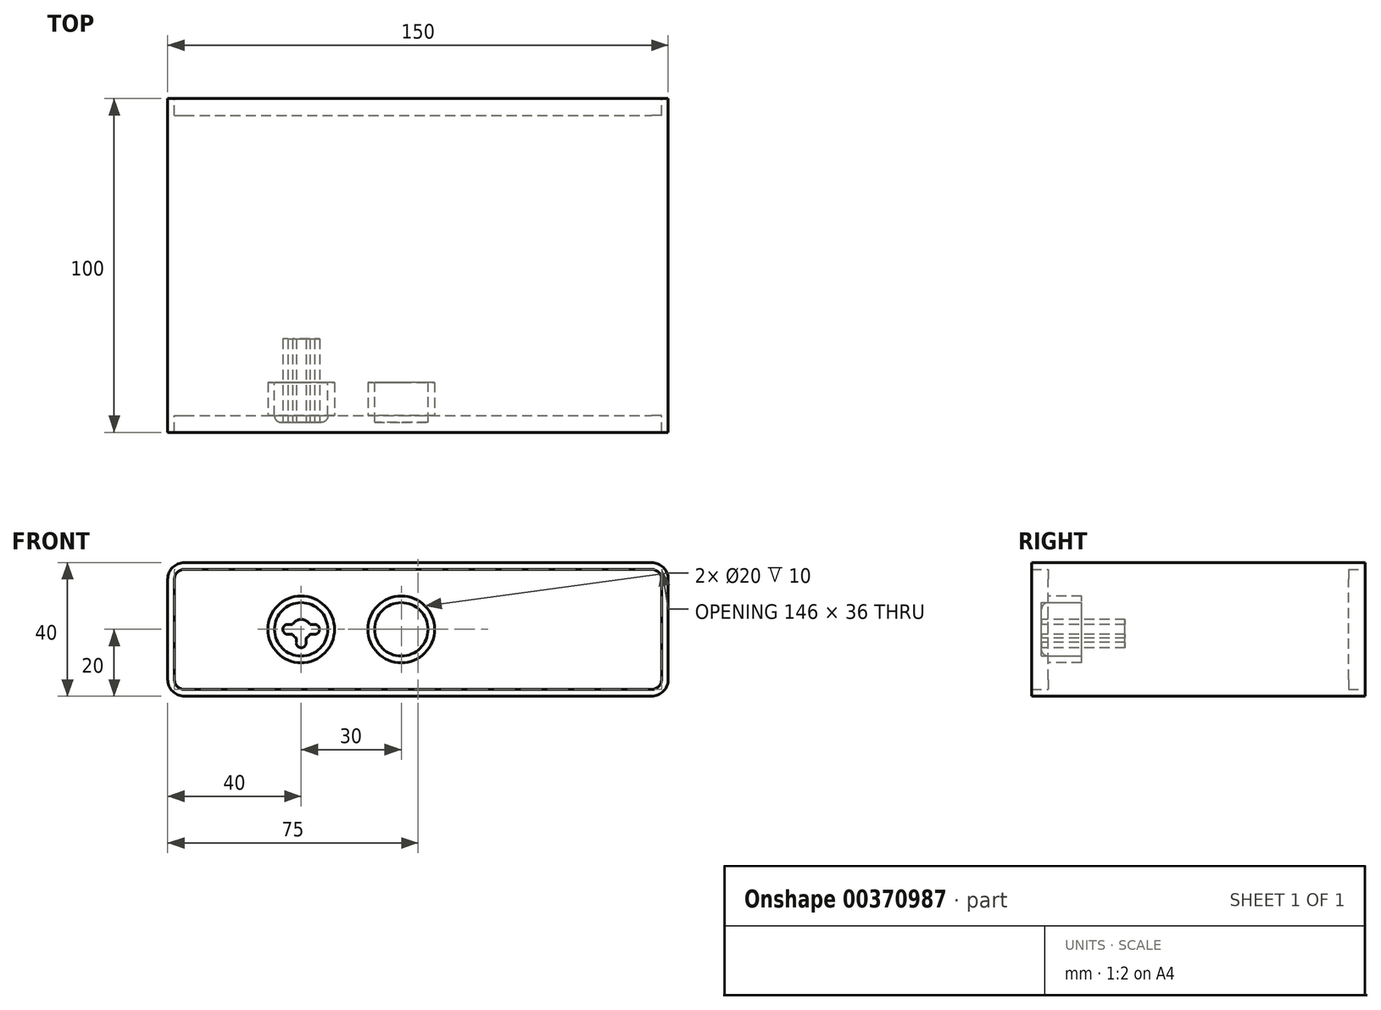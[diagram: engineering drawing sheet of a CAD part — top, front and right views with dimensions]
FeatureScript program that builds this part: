
annotation { "Feature Type Name" : "Feature", "Feature Type Description" : "" }
export const myFeature = defineFeature(function(context is Context, id is Id, definition is map)
    precondition{}
    {
        {
            var Q0;
            Q0=qCreatedBy(makeId("Front.planeOp"),FACE);
            var sketch = newSketch(context, id + "F0", { "sketchPlane" : qUnion([Q0])});
            skLineSegment(sketch, "E0.bottom", {"start": v(-70, -20) * mm, "end": v(70, -20) * mm});
            skLineSegment(sketch, "E0.top", {"start": v(-70, 20) * mm, "end": v(70, 20) * mm});
            skLineSegment(sketch, "E0.left", {"start": v(-75, -15) * mm, "end": v(-75, 15) * mm});
            skLineSegment(sketch, "E0.right", {"start": v(75, -15) * mm, "end": v(75, 15) * mm});
            skPoint(sketch, "E0.middle", {"position": v(0, 0) * mm});
            skPoint(sketch, "E1.visualSharp", {"position": v(-75, 20) * mm});
            skArc(sketch, "E1.filletArc", {"start": v(-70, 20) * mm, "mid": v(-73.54, 18.54) * mm, "end": v(-75, 15) * mm});
            skPoint(sketch, "E2.visualSharp", {"position": v(-75, -20) * mm});
            skArc(sketch, "E2.filletArc", {"start": v(-75, -15) * mm, "mid": v(-73.54, -18.54) * mm, "end": v(-70, -20) * mm});
            skPoint(sketch, "E3.visualSharp", {"position": v(75, -20) * mm});
            skArc(sketch, "E3.filletArc", {"start": v(70, -20) * mm, "mid": v(73.54, -18.54) * mm, "end": v(75, -15) * mm});
            skPoint(sketch, "E4.visualSharp", {"position": v(75, 20) * mm});
            skArc(sketch, "E4.filletArc", {"start": v(75, 15) * mm, "mid": v(73.54, 18.54) * mm, "end": v(70, 20) * mm});
            skLineSegment(sketch, "E5.0", {"start": v(73, -15) * mm, "end": v(73, 15) * mm});
            skLineSegment(sketch, "E5.1", {"start": v(-70, -18) * mm, "end": v(70, -18) * mm});
            skLineSegment(sketch, "E5.2", {"start": v(-73, -15) * mm, "end": v(-73, 15) * mm});
            skLineSegment(sketch, "E5.3", {"start": v(-70, 18) * mm, "end": v(70, 18) * mm});
            skPoint(sketch, "E6.visualSharp", {"position": v(-73, 18) * mm});
            skArc(sketch, "E6.filletArc", {"start": v(-70, 18) * mm, "mid": v(-72.12, 17.12) * mm, "end": v(-73, 15) * mm});
            skPoint(sketch, "E7.visualSharp", {"position": v(-73, -18) * mm});
            skArc(sketch, "E7.filletArc", {"start": v(-73, -15) * mm, "mid": v(-72.12, -17.12) * mm, "end": v(-70, -18) * mm});
            skPoint(sketch, "E8.visualSharp", {"position": v(73, -18) * mm});
            skArc(sketch, "E8.filletArc", {"start": v(70, -18) * mm, "mid": v(72.12, -17.12) * mm, "end": v(73, -15) * mm});
            skPoint(sketch, "E9.visualSharp", {"position": v(73, 18) * mm});
            skArc(sketch, "E9.filletArc", {"start": v(73, 15) * mm, "mid": v(72.12, 17.12) * mm, "end": v(70, 18) * mm});
            skSolve(sketch);
        }
        {
            var Q0;
            Q0=makeQuery(id+"F0.imprint","IMPRINT",FACE,{"disambiguationData":[TD([[makeQuery(id+"F0.imprint","IMPRINT",EDGE,{"derivedFrom":sQuery(id+"F0.wireOp",EDGE,"E0.bottom")}),1.0]])]});
            extrude(context, id + "F1", {"entities" : qUnion([Q0]), "endBound" : BoundingType.SYMMETRIC, "depth" : 100 * mm});
        }
        {
            var Q0;
            Q0=qCreatedBy(makeId("Front.planeOp"),FACE);
            var sketch = newSketch(context, id + "F2", { "sketchPlane" : qUnion([Q0])});
            skLineSegment(sketch, "E10.0", {"start": v(-73, -15) * mm, "end": v(-73, 15) * mm});
            skArc(sketch, "E10.1", {"start": v(-70, 18) * mm, "mid": v(-72.12, 17.12) * mm, "end": v(-73, 15) * mm});
            skLineSegment(sketch, "E10.2", {"start": v(-70, 18) * mm, "end": v(70, 18) * mm});
            skArc(sketch, "E10.3", {"start": v(-73, -15) * mm, "mid": v(-72.12, -17.12) * mm, "end": v(-70, -18) * mm});
            skLineSegment(sketch, "E10.4", {"start": v(-70, -18) * mm, "end": v(70, -18) * mm});
            skArc(sketch, "E10.5", {"start": v(70, -18) * mm, "mid": v(72.12, -17.12) * mm, "end": v(73, -15) * mm});
            skLineSegment(sketch, "E10.6", {"start": v(73, -15) * mm, "end": v(73, 15) * mm});
            skArc(sketch, "E10.7", {"start": v(73, 15) * mm, "mid": v(72.12, 17.12) * mm, "end": v(70, 18) * mm});
            skPoint(sketch, "E10.8", {"position": v(-72.12, 17.12) * mm});
            skSolve(sketch);
        }
        {
            var Q0;
            Q0 = qSketchRegion(id + "F2", true);
            extrude(context, id + "F3", {"entities" : qUnion([Q0]), "operationType" : NewBodyOperationType.ADD, "endBound" : BoundingType.SYMMETRIC, "depth" : 90 * mm});
        }
        {
            var Q0;
            Q0=makeQuery(id+"F3.opExtrude","CAP_FACE",FACE,{"disambiguationData":[OSD([sQuery(id+"F2.wireOp",EDGE,"E10.0"),sQuery(id+"F2.wireOp",EDGE,"E10.1"),sQuery(id+"F2.wireOp",EDGE,"E10.2"),sQuery(id+"F2.wireOp",EDGE,"E10.3"),sQuery(id+"F2.wireOp",EDGE,"E10.4"),sQuery(id+"F2.wireOp",EDGE,"E10.5"),sQuery(id+"F2.wireOp",EDGE,"E10.6"),sQuery(id+"F2.wireOp",EDGE,"E10.7")])],"isStart":false});
            var sketch = newSketch(context, id + "F4", { "sketchPlane" : qUnion([Q0])});
            skCircle(sketch, "E11", {"center": v(-35, 0) * mm, "radius": 10 * mm});
            skCircle(sketch, "E12", {"center": v(-5, 0) * mm, "radius": 10 * mm});
            skSolve(sketch);
        }
        {
            var Q0;
            Q0 = qSketchRegion(id + "F4", true);
            extrude(context, id + "F5", {"entities" : qUnion([Q0]), "operationType" : NewBodyOperationType.REMOVE, "oppositeDirection" : true, "depth" : 10 * mm});
        }
        {
            var Q0;
            Q0=makeQuery(id+"F5.boolean.opBoolean","COPY",FACE,{"derivedFrom":makeQuery(id+"F5.opExtrude","CAP_FACE",FACE,{"disambiguationData":[OSD([sQuery(id+"F4.wireOp",EDGE,"E11")])],"isStart":false})});
            var sketch = newSketch(context, id + "F6", { "sketchPlane" : qUnion([Q0])});
            skCircle(sketch, "E13.0", {"center": v(-5, 0) * mm, "radius": 8 * mm});
            skCircle(sketch, "E14.0", {"center": v(-35, 0) * mm, "radius": 8 * mm});
            skSolve(sketch);
        }
        {
            var Q0;
            Q0 = qSketchRegion(id + "F6", true);
            extrude(context, id + "F7", {"entities" : qUnion([Q0]), "operationType" : NewBodyOperationType.ADD, "depth" : 12 * mm});
        }
        {
            var Q0;
            Q0=makeQuery(id+"F7.opExtrude","CAP_FACE",FACE,{"disambiguationData":[OSD([sQuery(id+"F6.wireOp",EDGE,"E14.0")])],"isStart":false});
            var sketch = newSketch(context, id + "F8", { "sketchPlane" : qUnion([Q0])});
            skArc(sketch, "E15.0", {"start": v(-37.6, -1.5) * mm, "mid": v(-37.12, -2.12) * mm, "end": v(-36.5, -2.6) * mm});
            skArc(sketch, "E16", {"start": v(-38.97, 1.5) * mm, "mid": v(-40.5, 0) * mm, "end": v(-38.97, -1.5) * mm});
            skArc(sketch, "E17", {"start": v(-31.03, -1.5) * mm, "mid": v(-29.5, -0.01) * mm, "end": v(-31, 1.5) * mm});
            skArc(sketch, "E18", {"start": v(-36.5, -3.92) * mm, "mid": v(-35.01, -5.5) * mm, "end": v(-33.5, -3.94) * mm});
            skLineSegment(sketch, "E19", {"start": v(-38.97, 1.5) * mm, "end": v(-37.6, 1.5) * mm});
            skLineSegment(sketch, "E20", {"start": v(-38.97, -1.5) * mm, "end": v(-37.6, -1.5) * mm});
            skLineSegment(sketch, "E21", {"start": v(-36.5, -4.08) * mm, "end": v(-36.5, -2.6) * mm});
            skLineSegment(sketch, "E22", {"start": v(-33.5, -4.06) * mm, "end": v(-33.5, -2.6) * mm});
            skArc(sketch, "E23.trimOffspring", {"start": v(-32.4, 1.5) * mm, "mid": v(-35, 3) * mm, "end": v(-37.6, 1.5) * mm});
            skLineSegment(sketch, "E24.trimOffspring", {"start": v(-32.4, -1.5) * mm, "end": v(-30.97, -1.5) * mm});
            skArc(sketch, "E25.trimOffspring", {"start": v(-33.5, -2.6) * mm, "mid": v(-32.88, -2.12) * mm, "end": v(-32.4, -1.5) * mm});
            skLineSegment(sketch, "E26.trimOffspring", {"start": v(-32.4, 1.5) * mm, "end": v(-31, 1.5) * mm});
            skSolve(sketch);
        }
        {
            var Q0;
            Q0 = qSketchRegion(id + "F8", true);
            extrude(context, id + "F9", {"entities" : qUnion([Q0]), "operationType" : NewBodyOperationType.REMOVE, "oppositeDirection" : true, "depth" : 25 * mm});
        }
        {
            var Q0;
            Q0=makeQuery(id+"F7.opExtrude","CAP_EDGE",EDGE,{"disambiguationData":[OSD([sQuery(id+"F6.wireOp",EDGE,"E14.0")])],"isStart":false});
            fillet(context, id + "F10", {"entities" : qUnion([Q0]), "radius" : 2 * mm, "tangentPropagation" : true, "allowEdgeOverflow" : false});
        }
    });
